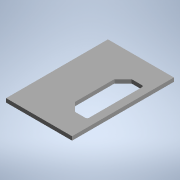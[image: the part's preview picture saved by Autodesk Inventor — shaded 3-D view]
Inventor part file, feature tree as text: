
AUTODESK INVENTOR PART (.ipt)
format: ipt  version: 2020 (Build 240168000, 168)  size: 184,832 bytes
history: native  units: mm
features: extrude x1
ambient origin geometry x8: Origin, YZ Plane, XZ Plane, XY Plane, X Axis, Y Axis, Z Axis, Center Point
bodies: Solid1 (feature_tree)
feature tree (1):
  extrude  "Extrusion1"  Depth=10.0mm
